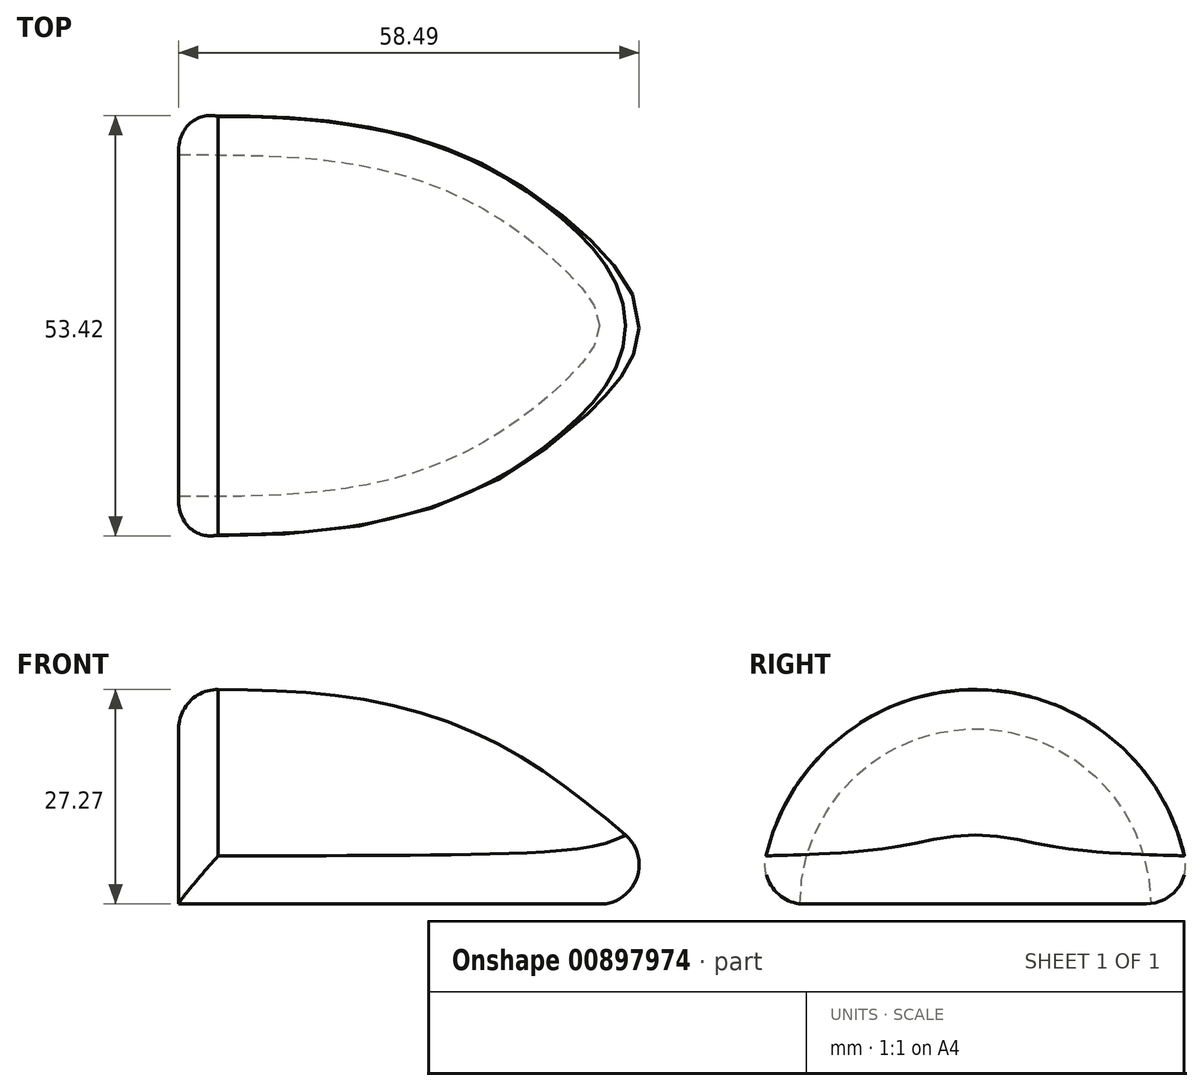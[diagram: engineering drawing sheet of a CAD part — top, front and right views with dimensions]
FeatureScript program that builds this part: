
annotation { "Feature Type Name" : "Feature", "Feature Type Description" : "" }
export const myFeature = defineFeature(function(context is Context, id is Id, definition is map)
    precondition{}
    {
        {
            var Q0;
            Q0=qCreatedBy(makeId("Right.planeOp"),FACE);
            var sketch = newSketch(context, id + "F0", { "sketchPlane" : qUnion([Q0])});
            skArc(sketch, "E0", {"start": v(27.27, 0) * mm, "mid": v(0, 27.27) * mm, "end": v(-27.27, 0) * mm});
            skLineSegment(sketch, "E1", {"start": v(0, 0) * mm, "end": v(-27.27, 0) * mm});
            skLineSegment(sketch, "E2", {"start": v(0, 0) * mm, "end": v(27.27, 0) * mm});
            skSolve(sketch);
        }
        {
            var Q0;
            Q0=qCreatedBy(makeId("Right.planeOp"),FACE);
            cPlane(context, id + "F1", {"entities" : qUnion([Q0]), "cplaneType" : CPlaneType.OFFSET, "offset" : 42.32 * mm, "width" : 150 * mm, "height" : 150 * mm});
        }
        {
            var Q0;
            Q0=qCreatedBy(id+"F1.planeOp",FACE);
            var sketch = newSketch(context, id + "F2", { "sketchPlane" : qUnion([Q0])});
            skLineSegment(sketch, "E3", {"start": v(0, 0) * mm, "end": v(0, 0) * mm});
            skLineSegment(sketch, "E4", {"start": v(0, 0) * mm, "end": v(-19.37, 0) * mm});
            skLineSegment(sketch, "E5", {"start": v(0, 0) * mm, "end": v(19.37, 0) * mm});
            skArc(sketch, "E6", {"start": v(19.37, 0) * mm, "mid": v(0, 19.37) * mm, "end": v(-19.37, 0) * mm});
            skSolve(sketch);
        }
        {
            var Q0;
            Q0 = qBodyType(qCreatedBy(id + "FNI2DpFX9WuRNIP_0" ,EDGE), BodyType.WIRE);
            var Q1;
            Q1=qCreatedBy(id+"F1.planeOp",FACE);
            cPlane(context, id + "F3", {"entities" : qUnion([Q0, Q1]), "cplaneType" : CPlaneType.OFFSET, "offset" : 24.25 * mm, "width" : 150 * mm, "height" : 150 * mm});
        }
        {
            var Q0;
            Q0=qCreatedBy(id+"F3.planeOp",FACE);
            var sketch = newSketch(context, id + "F4", { "sketchPlane" : qUnion([Q0])});
            skPoint(sketch, "E7.0", {"position": v(0, 0) * mm});
            skSolve(sketch);
        }
        {
            var Q0;
            Q0=makeQuery(id+"F0.imprint","IMPRINT",FACE,{"disambiguationData":[TD([[makeQuery(id+"F0.imprint","IMPRINT",EDGE,{"derivedFrom":sQuery(id+"F0.wireOp",EDGE,"E0")}),1.0]])]});
            var Q1;
            Q1=makeQuery(id+"F2.imprint","IMPRINT",FACE,{"disambiguationData":[TD([[makeQuery(id+"F2.imprint","IMPRINT",EDGE,{"derivedFrom":sQuery(id+"F2.wireOp",EDGE,"E4")}),-1.0]])]});
            var Q2;
            Q2=sQuery(id+"F4.wireOp",VERTEX,"E7.0");
            var Q3;
            Q3=sQuery(id+"F0.wireOp",EDGE,"E0");
            var Q4;
            Q4=makeQuery(id+"F0.imprint","IMPRINT",FACE,{"disambiguationData":[TD([[makeQuery(id+"F0.imprint","IMPRINT",EDGE,{"derivedFrom":sQuery(id+"F0.wireOp",EDGE,"E0")}),1.0]])]});
            var Q5;
            Q5=sQuery(id+"F2.wireOp",EDGE,"E5");
            var Q6;
            Q6=makeQuery(id+"F2.imprint","IMPRINT",FACE,{"disambiguationData":[TD([[makeQuery(id+"F2.imprint","IMPRINT",EDGE,{"derivedFrom":sQuery(id+"F2.wireOp",EDGE,"E4")}),-1.0]])]});
            var Q7;
            Q7=sQuery(id+"F4.wireOp",VERTEX,"E7.0");
            loft(context, id + "F5", {"sheetProfilesArray" : [{ "sheetProfileEntities" : qUnion([Q0]) }, { "sheetProfileEntities" : qUnion([Q1]) }, { "sheetProfileEntities" : qUnion([Q2]) }], "wireProfilesArray" : [{ "wireProfileEntities" : qUnion([Q3]) }, { "wireProfileEntities" : qUnion([Q4]) }, { "wireProfileEntities" : qUnion([Q5]) }, { "wireProfileEntities" : qUnion([Q6]) }, { "wireProfileEntities" : qUnion([Q7]) }]});
        }
        {
            var Q0;
            {var subQ0=sQuery(id+"F2.wireOp",EDGE,"E6");var subQ1=sQuery(id+"F2.wireOp",EDGE,"E5");var subQ2=sQuery(id+"F2.wireOp",EDGE,"E4");var subQ3=sQuery(id+"F0.wireOp",EDGE,"E0");var subQ4=sQuery(id+"F0.wireOp",EDGE,"E1");var subQ5=sQuery(id+"F0.wireOp",EDGE,"E2");Q0=makeQuery(id+"F5.opLoft","SWEPT_FACE",FACE,{"disambiguationData":[OSD([subQ3,subQ4,subQ5,subQ2,subQ1,subQ0]),TDD([makeQuery(id+"F0.imprint","INTERSECT",VERTEX,{"derivedFrom":[subQ3,subQ5]}),makeQuery(id+"F0.imprint","INTERSECT",VERTEX,{"derivedFrom":[subQ3,subQ4]}),makeQuery(id+"F0.imprint","IMPRINT",EDGE,{"derivedFrom":subQ3}),makeQuery(id+"F2.imprint","INTERSECT",VERTEX,{"derivedFrom":[subQ2,subQ0]}),makeQuery(id+"F2.imprint","INTERSECT",VERTEX,{"derivedFrom":[subQ1,subQ0]}),makeQuery(id+"F2.imprint","IMPRINT",EDGE,{"derivedFrom":subQ0})])]});}
            fillet(context, id + "F6", {"entities" : qUnion([Q0]), "radius" : 5 * mm, "tangentPropagation" : true, "allowEdgeOverflow" : false});
        }
    });
